# Revit family: Kugelhahn mit Hebelgriff (Blech) 2201
name_source: partatom
category: Rohrzubehör
units: mm (PartAtom-declared; Revit-internal decimal feet)

## family parameters
Arbeitsebenenbasiert = Nein
Beim Laden mit Abzugskörper schneiden = Nein
Bemaßung runder Anschluss = Durchmesser verwenden
Gemeinsam genutzt = Nein
Immer vertikal = Ja
OmniClass-Nummer = 23.65.55.14
OmniClass-Titel = Valves for Liquid Services
Teiletyp = Unterbricht

## types (1)
- Kugelhahn mit Hebelgriff (Blech) 2201
    Anwendungen = Der Kugelhahn wird in der Installation als Absperreinrichtung verwendet.
Anwendungsgebiete sind Zentralheizungs- und Kälteanlagenlagen.
Die Betriebsbedingungen (wie Temperatur und Druck) sollten dabei eingehalten werden.
    Einsatzbereich = Kugelhähne werden zum Absperren von Leitungen und Anlagen verwendet.
Einsatzbereiche sind Heizungs- und Kälteanlagen.
Der Kugelhahn ist nicht geeignet für die Durchflussregelung und muss immer in voll geöffneter oder geschlossener Position verwendet werden.
    Gehäuse = geschmiedetes Messing nach EN 12165, vernickelt, CW617N
    Griff = Hebelgriff rot, Stahlblech beschichtet
    Hersteller = HERZ Armaturen Ges.m.b.H
    Innengewinde = nach ISO 228-1
    Kugel = geschmiedetes Messing nach EN 12165, voller Durchgang, verchromt, CW617N
    Kugeldichtung = PTFE
    Max.Betriebsdruck = 2500000.0 Pa
    Max.Betriebsdruck (Verschraubung) = 1600000.0 Pa
    Max.Betriebstemperatur = 150 °C
    Max.Betriebstemperatur (Wasser - kein Dampf) = 110 °C
    Medium = Heizungswasserqualität nach ÖNORM H 5195 oder VDI-Richtline 2035.
Die Verwendung von Ethylen- oder Propylenglykol in einem Mischungsverhältnis 25 - 50% ist zulässig.
    Min.Betriebstemperatur = -30 °C
    Min.Betriebstemperatur (Wasser) = 1 °C
    SCRNCODE = 05;10;02
    SCRNSEQ = ARM;ARM_TYP="ABVS";2
    Spindel = Messing nach EN 12164, CW614N
    Spindeldichtung = PTFE
    URL = www.herz-armaturen.at
    W01 = 135.00°
